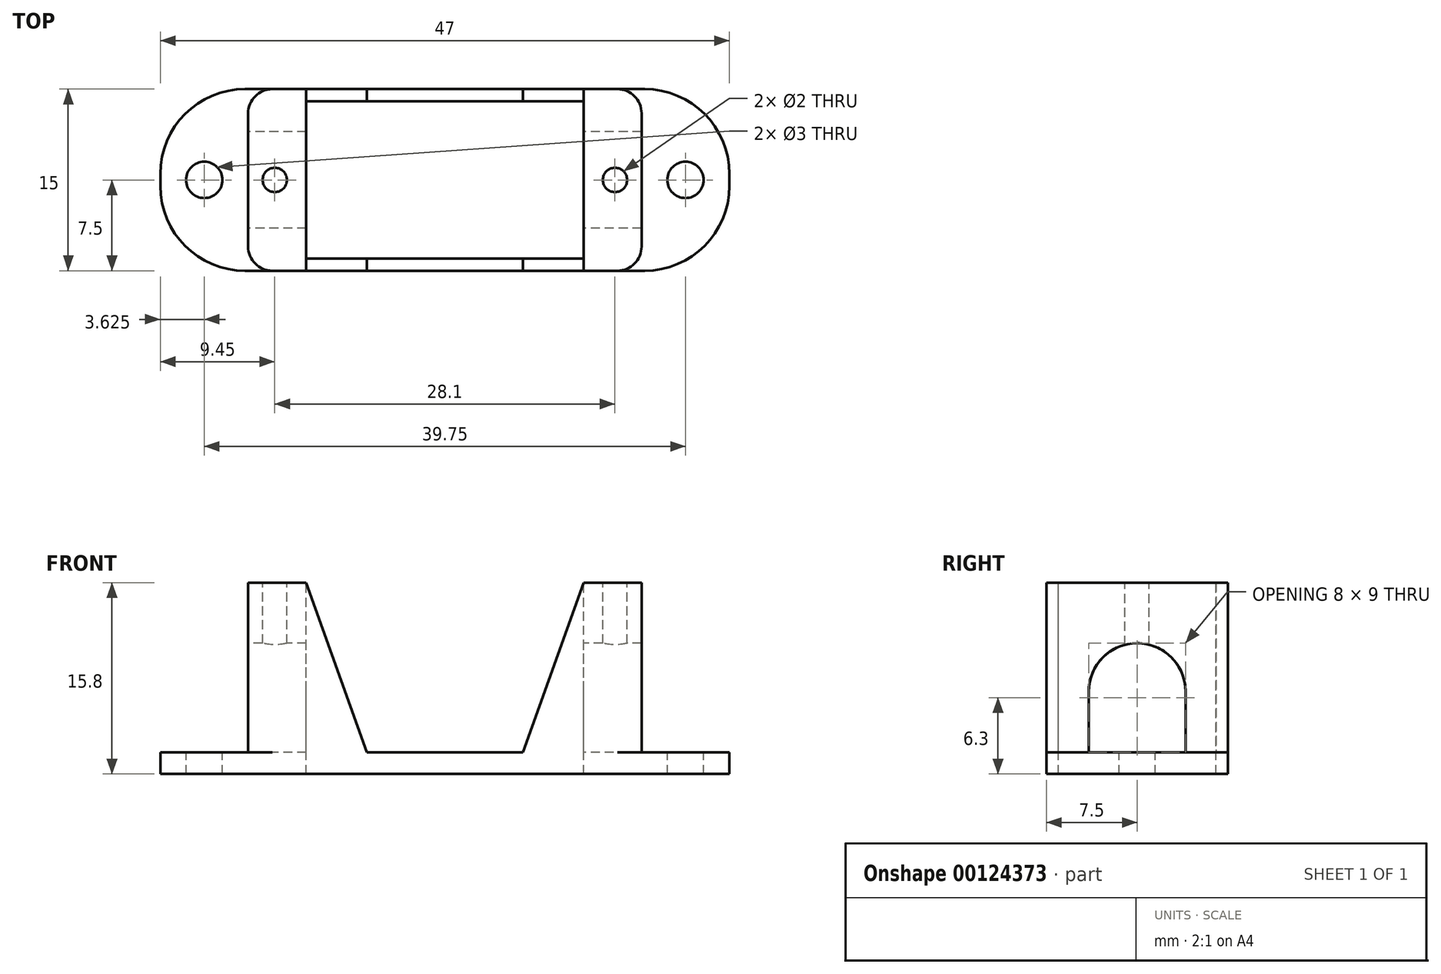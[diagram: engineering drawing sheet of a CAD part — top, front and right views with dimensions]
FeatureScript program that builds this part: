
annotation { "Feature Type Name" : "Feature", "Feature Type Description" : "" }
export const myFeature = defineFeature(function(context is Context, id is Id, definition is map)
    precondition{}
    {
        {
            var Q0;
            Q0=qCreatedBy(makeId("Top.planeOp"),FACE);
            var sketch = newSketch(context, id + "F0", { "sketchPlane" : qUnion([Q0])});
            skLineSegment(sketch, "E0.bottom", {"start": v(0, 0) * mm, "end": v(47, 0) * mm});
            skLineSegment(sketch, "E0.top", {"start": v(0, 15) * mm, "end": v(47, 15) * mm});
            skLineSegment(sketch, "E0.left", {"start": v(0, 0) * mm, "end": v(0, 15) * mm});
            skLineSegment(sketch, "E0.right", {"start": v(47, 0) * mm, "end": v(47, 15) * mm});
            skSolve(sketch);
        }
        {
            var Q0;
            Q0=makeQuery(id+"F0.imprint","IMPRINT",FACE,{"disambiguationData":[TD([[makeQuery(id+"F0.imprint","IMPRINT",EDGE,{"derivedFrom":sQuery(id+"F0.wireOp",EDGE,"E0.bottom")}),1.0]])]});
            extrude(context, id + "F1", {"entities" : qUnion([Q0]), "depth" : 1.8 * mm});
        }
        {
            var Q0;
            Q0=makeQuery(id+"F1.opExtrude","CAP_FACE",FACE,{"disambiguationData":[OSD([sQuery(id+"F0.wireOp",EDGE,"E0.bottom"),sQuery(id+"F0.wireOp",EDGE,"E0.top"),sQuery(id+"F0.wireOp",EDGE,"E0.left"),sQuery(id+"F0.wireOp",EDGE,"E0.right")])],"isStart":false});
            var sketch = newSketch(context, id + "F2", { "sketchPlane" : qUnion([Q0])});
            skLineSegment(sketch, "E1", {"start": v(23.5, 15) * mm, "end": v(23.5, 0) * mm, "construction": true});
            skLineSegment(sketch, "E2", {"start": v(23.5, 15) * mm, "end": v(7.25, 15) * mm});
            skLineSegment(sketch, "E3", {"start": v(7.25, 15) * mm, "end": v(7.25, 0) * mm});
            skLineSegment(sketch, "E4", {"start": v(7.25, 0) * mm, "end": v(23.5, 0) * mm});
            skLineSegment(sketch, "E5.MirrorCS", {"start": v(23.5, 15) * mm, "end": v(39.75, 15) * mm});
            skLineSegment(sketch, "E6.MirrorCS", {"start": v(39.75, 0) * mm, "end": v(23.5, 0) * mm});
            skLineSegment(sketch, "E7.MirrorCS", {"start": v(39.75, 15) * mm, "end": v(39.75, 0) * mm});
            skSolve(sketch);
        }
        {
            var Q0;
            Q0 = qSketchRegion(id + "F2", true);
            extrude(context, id + "F3", {"entities" : qUnion([Q0]), "operationType" : NewBodyOperationType.ADD, "depth" : 14 * mm});
        }
        {
            var Q0;
            Q0=makeQuery(id+"F3.opExtrude","CAP_FACE",FACE,{"disambiguationData":[OSD([sQuery(id+"F2.wireOp",EDGE,"E2"),sQuery(id+"F2.wireOp",EDGE,"E3"),sQuery(id+"F2.wireOp",EDGE,"E4"),sQuery(id+"F2.wireOp",EDGE,"E5.MirrorCS"),sQuery(id+"F2.wireOp",EDGE,"E6.MirrorCS"),sQuery(id+"F2.wireOp",EDGE,"E7.MirrorCS")])],"isStart":false});
            var sketch = newSketch(context, id + "F4", { "sketchPlane" : qUnion([Q0])});
            skLineSegment(sketch, "E8.bottom", {"start": v(12.05, 14) * mm, "end": v(34.95, 14) * mm});
            skLineSegment(sketch, "E8.top", {"start": v(12.05, 1) * mm, "end": v(34.95, 1) * mm});
            skLineSegment(sketch, "E8.left", {"start": v(12.05, 14) * mm, "end": v(12.05, 1) * mm});
            skLineSegment(sketch, "E8.right", {"start": v(34.95, 14) * mm, "end": v(34.95, 1) * mm});
            skSolve(sketch);
        }
        {
            var Q0;
            Q0 = qSketchRegion(id + "F4", true);
            extrude(context, id + "F5", {"entities" : qUnion([Q0]), "operationType" : NewBodyOperationType.REMOVE, "endBound" : BoundingType.THROUGH_ALL, "oppositeDirection" : true, "depth" : 25 * mm});
        }
        {
            var Q0;
            Q0=makeQuery(id+"F3.opExtrude","CAP_FACE",FACE,{"disambiguationData":[OSD([sQuery(id+"F2.wireOp",EDGE,"E2"),sQuery(id+"F2.wireOp",EDGE,"E3"),sQuery(id+"F2.wireOp",EDGE,"E4"),sQuery(id+"F2.wireOp",EDGE,"E5.MirrorCS"),sQuery(id+"F2.wireOp",EDGE,"E6.MirrorCS"),sQuery(id+"F2.wireOp",EDGE,"E7.MirrorCS")])],"isStart":false});
            var sketch = newSketch(context, id + "F6", { "sketchPlane" : qUnion([Q0])});
            skCircle(sketch, "E9", {"center": v(9.45, 7.5) * mm, "radius": 1 * mm});
            skPoint(sketch, "E9.centerSnap0", {"position": v(7.25, 7.5) * mm});
            skLineSegment(sketch, "E10", {"start": v(23.5, 15) * mm, "end": v(23.5, 0) * mm, "construction": true});
            skCircle(sketch, "E11.MirrorC", {"center": v(37.55, 7.5) * mm, "radius": 1 * mm});
            skSolve(sketch);
        }
        {
            var Q0;
            Q0 = qSketchRegion(id + "F6", true);
            extrude(context, id + "F7", {"entities" : qUnion([Q0]), "operationType" : NewBodyOperationType.REMOVE, "oppositeDirection" : true, "depth" : 7 * mm});
        }
        {
            var Q0;
            {var subQ0=sQuery(id+"F0.wireOp",EDGE,"E0.left");var subQ1=sQuery(id+"F0.wireOp",EDGE,"E0.top");var subQ2=sQuery(id+"F0.wireOp",EDGE,"E0.bottom");Q0=makeQuery(id+"F3.boolean.opBoolean","SPLIT",FACE,{"disambiguationData":[TD([makeQuery(id+"F1.opExtrude","SWEPT_FACE",FACE,{"disambiguationData":[OSD([subQ0])]})])],"derivedFrom":makeQuery(id+"F1.opExtrude","CAP_FACE",FACE,{"disambiguationData":[OSD([subQ2,subQ1,subQ0,sQuery(id+"F0.wireOp",EDGE,"E0.right")])],"isStart":false})});}
            var sketch = newSketch(context, id + "F8", { "sketchPlane" : qUnion([Q0])});
            skCircle(sketch, "E12", {"center": v(3.63, 7.5) * mm, "radius": 1.5 * mm});
            skPoint(sketch, "E12.centerSnap0", {"position": v(3.63, 15) * mm});
            skPoint(sketch, "E12.centerSnap1", {"position": v(0, 7.5) * mm});
            skSolve(sketch);
        }
        {
            var Q0;
            {var subQ0=sQuery(id+"F0.wireOp",EDGE,"E0.right");var subQ1=sQuery(id+"F0.wireOp",EDGE,"E0.top");var subQ2=sQuery(id+"F0.wireOp",EDGE,"E0.bottom");Q0=makeQuery(id+"F3.boolean.opBoolean","SPLIT",FACE,{"disambiguationData":[TD([makeQuery(id+"F1.opExtrude","SWEPT_FACE",FACE,{"disambiguationData":[OSD([subQ0])]})])],"derivedFrom":makeQuery(id+"F1.opExtrude","CAP_FACE",FACE,{"disambiguationData":[OSD([subQ2,subQ1,sQuery(id+"F0.wireOp",EDGE,"E0.left"),subQ0])],"isStart":false})});}
            var sketch = newSketch(context, id + "F9", { "sketchPlane" : qUnion([Q0])});
            skCircle(sketch, "E13", {"center": v(43.38, 7.5) * mm, "radius": 1.5 * mm});
            skPoint(sketch, "E13.centerSnap0", {"position": v(43.38, 15) * mm});
            skPoint(sketch, "E13.centerSnap1", {"position": v(47, 7.5) * mm});
            skSolve(sketch);
        }
        {
            var Q0;
            Q0 = qSketchRegion(id + "F8", true);
            var Q1;
            Q1 = qSketchRegion(id + "F9", true);
            extrude(context, id + "F10", {"entities" : qUnion([Q0, Q1]), "operationType" : NewBodyOperationType.REMOVE, "endBound" : BoundingType.THROUGH_ALL, "oppositeDirection" : true, "depth" : 25 * mm});
        }
        {
            var Q0;
            Q0=makeQuery(id+"F3.opExtrude","SWEPT_FACE",FACE,{"disambiguationData":[OSD([sQuery(id+"F2.wireOp",EDGE,"E3")])]});
            var sketch = newSketch(context, id + "F11", { "sketchPlane" : qUnion([Q0])});
            skLineSegment(sketch, "E14", {"start": v(0, 15.8) * mm, "end": v(0, 1.8) * mm});
            skLineSegment(sketch, "E15", {"start": v(-1, 15.8) * mm, "end": v(0, 15.8) * mm});
            skPoint(sketch, "E16.centerSnap0", {"position": v(-7.5, 1.8) * mm});
            skLineSegment(sketch, "E17", {"start": v(-11.5, 1.8) * mm, "end": v(-11.5, 6.8) * mm});
            skLineSegment(sketch, "E18", {"start": v(-11.5, 1.8) * mm, "end": v(-3.5, 1.8) * mm});
            skLineSegment(sketch, "E19", {"start": v(-11.5, 6.8) * mm, "end": v(-11.5, 6.8) * mm});
            skArc(sketch, "E20", {"start": v(-3.5, 6.8) * mm, "mid": v(-7.5, 10.8) * mm, "end": v(-11.5, 6.8) * mm});
            skLineSegment(sketch, "E21", {"start": v(-3.5, 6.8) * mm, "end": v(-3.5, 1.8) * mm});
            skLineSegment(sketch, "E22", {"start": v(-3.5, 6.8) * mm, "end": v(-3.5, 6.8) * mm});
            skSolve(sketch);
        }
        {
            var Q0;
            Q0=makeQuery(id+"F11.imprint","IMPRINT",FACE,{"disambiguationData":[TD([[makeQuery(id+"F11.imprint","IMPRINT",EDGE,{"derivedFrom":sQuery(id+"F11.wireOp",EDGE,"E17")}),-1.0]])]});
            extrude(context, id + "F12", {"entities" : qUnion([Q0]), "operationType" : NewBodyOperationType.REMOVE, "endBound" : BoundingType.THROUGH_ALL, "oppositeDirection" : true, "depth" : 25 * mm});
        }
        {
            var Q0;
            Q0=makeQuery(id+"F1.opExtrude","SWEPT_EDGE",EDGE,{"disambiguationData":[OSD([sQuery(id+"F0.wireOp",EDGE,"E0.top"),sQuery(id+"F0.wireOp",EDGE,"E0.left")])]});
            var Q1;
            Q1=makeQuery(id+"F1.opExtrude","SWEPT_EDGE",EDGE,{"disambiguationData":[OSD([sQuery(id+"F0.wireOp",EDGE,"E0.bottom"),sQuery(id+"F0.wireOp",EDGE,"E0.left")])]});
            var Q2;
            Q2=makeQuery(id+"F1.opExtrude","SWEPT_EDGE",EDGE,{"disambiguationData":[OSD([sQuery(id+"F0.wireOp",EDGE,"E0.bottom"),sQuery(id+"F0.wireOp",EDGE,"E0.right")])]});
            var Q3;
            Q3=makeQuery(id+"F1.opExtrude","SWEPT_EDGE",EDGE,{"disambiguationData":[OSD([sQuery(id+"F0.wireOp",EDGE,"E0.top"),sQuery(id+"F0.wireOp",EDGE,"E0.right")])]});
            fillet(context, id + "F13", {"entities" : qUnion([Q0, Q1, Q2, Q3]), "radius" : 7 * mm, "tangentPropagation" : true, "allowEdgeOverflow" : false});
        }
        {
            var Q0;
            Q0=makeQuery(id+"F5.boolean.opBoolean","COPY",FACE,{"derivedFrom":makeQuery(id+"F5.opExtrude","SWEPT_FACE",FACE,{"disambiguationData":[OSD([sQuery(id+"F4.wireOp",EDGE,"E8.bottom")])]})});
            var sketch = newSketch(context, id + "F14", { "sketchPlane" : qUnion([Q0])});
            skLineSegment(sketch, "E23", {"start": v(12.05, 15.8) * mm, "end": v(34.95, 15.8) * mm});
            skLineSegment(sketch, "E24", {"start": v(34.95, 15.8) * mm, "end": v(29.95, 1.8) * mm});
            skLineSegment(sketch, "E25", {"start": v(29.95, 1.8) * mm, "end": v(17.05, 1.8) * mm});
            skLineSegment(sketch, "E26", {"start": v(17.05, 1.8) * mm, "end": v(12.05, 15.8) * mm});
            skSolve(sketch);
        }
        {
            var Q0;
            Q0=makeQuery(id+"F14.imprint","IMPRINT",FACE,{"disambiguationData":[TD([[makeQuery(id+"F14.imprint","IMPRINT",EDGE,{"derivedFrom":sQuery(id+"F14.wireOp",EDGE,"E23")}),-1.0]])]});
            extrude(context, id + "F15", {"entities" : qUnion([Q0]), "operationType" : NewBodyOperationType.REMOVE, "endBound" : BoundingType.THROUGH_ALL, "oppositeDirection" : true, "depth" : 25 * mm});
        }
        {
            var Q0;
            Q0 = qSketchRegion(id + "F14", true);
            extrude(context, id + "F16", {"entities" : qUnion([Q0]), "operationType" : NewBodyOperationType.REMOVE, "endBound" : BoundingType.THROUGH_ALL, "depth" : 25 * mm});
        }
        {
            var Q0;
            Q0=makeQuery(id+"F3.opExtrude","SWEPT_EDGE",EDGE,{"disambiguationData":[OSD([sQuery(id+"F0.wireOp",EDGE,"E0.top"),sQuery(id+"F2.wireOp",EDGE,"E5.MirrorCS"),sQuery(id+"F2.wireOp",EDGE,"E7.MirrorCS")])]});
            var Q1;
            Q1=makeQuery(id+"F3.opExtrude","SWEPT_EDGE",EDGE,{"disambiguationData":[OSD([sQuery(id+"F0.wireOp",EDGE,"E0.bottom"),sQuery(id+"F2.wireOp",EDGE,"E6.MirrorCS"),sQuery(id+"F2.wireOp",EDGE,"E7.MirrorCS")])]});
            var Q2;
            Q2=makeQuery(id+"F3.opExtrude","SWEPT_EDGE",EDGE,{"disambiguationData":[OSD([sQuery(id+"F0.wireOp",EDGE,"E0.bottom"),sQuery(id+"F2.wireOp",EDGE,"E3"),sQuery(id+"F2.wireOp",EDGE,"E4")])]});
            var Q3;
            Q3=makeQuery(id+"F3.opExtrude","SWEPT_EDGE",EDGE,{"disambiguationData":[OSD([sQuery(id+"F0.wireOp",EDGE,"E0.top"),sQuery(id+"F2.wireOp",EDGE,"E2"),sQuery(id+"F2.wireOp",EDGE,"E3")])]});
            fillet(context, id + "F17", {"entities" : qUnion([Q0, Q1, Q2, Q3]), "radius" : 2 * mm, "tangentPropagation" : true, "allowEdgeOverflow" : false});
        }
    });
